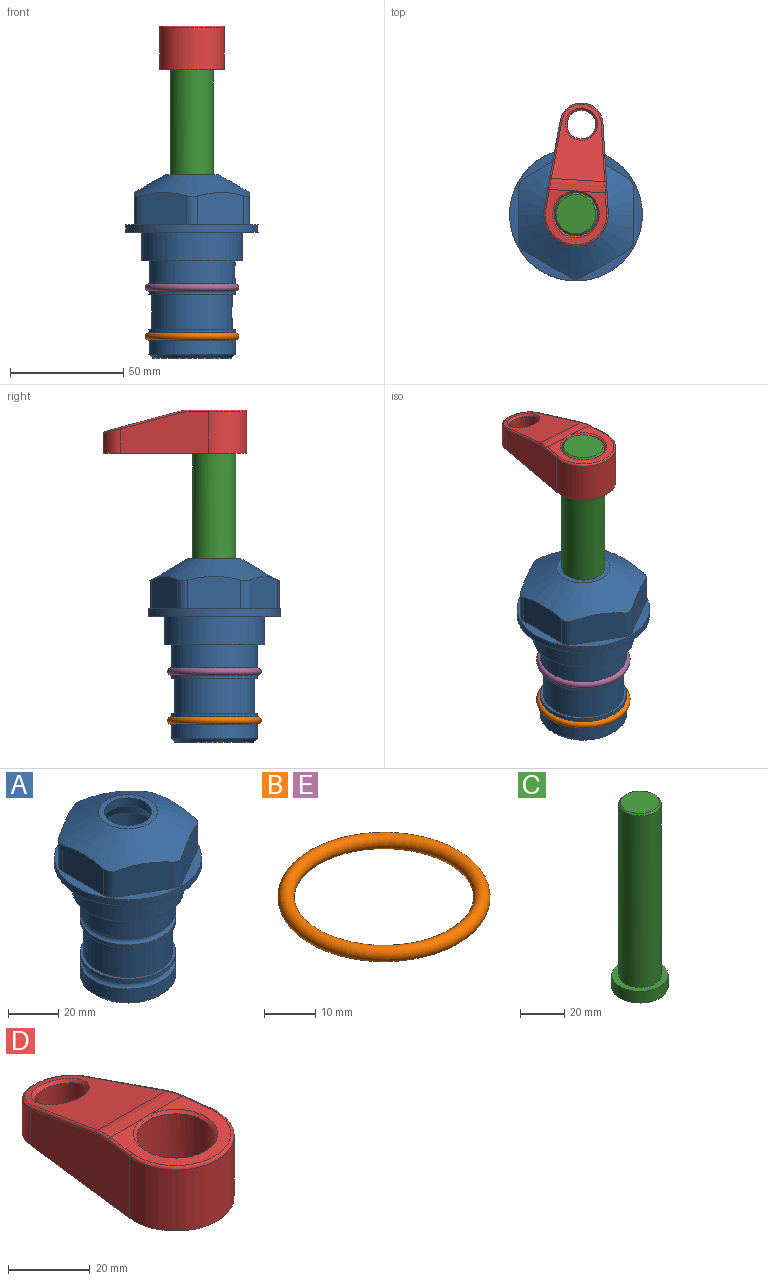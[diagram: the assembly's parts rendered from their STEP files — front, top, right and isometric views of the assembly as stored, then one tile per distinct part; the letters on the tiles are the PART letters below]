
ASSEMBLY  parts=5 mates=4
PART A: 36 faces, bbox 58.7x58.7x81 mm
  f0: cylinder r=17.78mm len=35.56mm, axis (0,0,1), area 1670.8mm2, adj f23,f24,f31
  f1: cylinder r=19.05mm len=38.1mm, axis (0,0,1), area 1191.9mm2, adj f26,f27,f30
  f2: plane 58.66x58.66mm, normal (0,0,-1), area 1150.6mm2, adj f3,f28
  f3: cylinder r=29.33mm len=58.66mm, axis (0,0,-1), area 585.1mm2, adj f2,f4
  f4: plane 58.66x58.66mm, normal (0,0,1), area 475.9mm2, adj f3,f5,f6,f7,f8,f9,f10,f11
  f5: plane 20.32x14.34mm, normal (-0.5,0.87,0), area 324.4mm2, adj f4,f15,f16,f17
  f6: plane 20.32x14.34mm, normal (0.5,0.87,0), area 324.4mm2, adj f4,f14,f15,f17
  f7: plane 23.48x14.34mm, normal (1,0,0), area 324.4mm2, adj f4,f13,f14,f17
  f8: plane 20.32x14.34mm, normal (0.5,-0.87,0), area 324.4mm2, adj f4,f12,f13,f17
  f9: plane 20.32x14.34mm, normal (-0.5,-0.87,0), area 324.4mm2, adj f4,f11,f12,f17
  f10: plane 23.48x14.34mm, normal (-1,0,0), area 324.4mm2, adj f4,f11,f16,f17
  f11: cylinder r=5.08mm len=12.85mm, axis (0,0,-1), area 67.2mm2, adj f4,f9,f10,f17
  f12: cylinder r=5.08mm len=12.85mm, axis (0,0,-1), area 67.2mm2, adj f4,f8,f9,f17
  f13: cylinder r=5.08mm len=12.85mm, axis (0,0,-1), area 67.2mm2, adj f4,f7,f8,f17
  f14: cylinder r=5.08mm len=12.85mm, axis (0,0,-1), area 67.2mm2, adj f4,f6,f7,f17
  f15: cylinder r=5.08mm len=12.85mm, axis (0,0,-1), area 67.2mm2, adj f4,f5,f6,f17
  f16: cylinder r=5.08mm len=12.85mm, axis (0,0,-1), area 67.2mm2, adj f4,f5,f10,f17
  f17: cone r=11.73mm half-angle=60deg, axis (0,0,-1), area 2071.8mm2, adj f5,f6,f7,f8,f9,f10,f11,f12
  f18: plane 23.46x23.46mm, normal (0,0,1), area 147.4mm2, adj f17,f35
  f19: plane 34.93x34.93mm, normal (0,0,-1), area 958mm2, adj f29
  f20: cylinder r=19.05mm len=38.1mm, axis (0,0,1), area 760.1mm2, adj f21,f29
  f21: torus R=19.05mm, axis (0,0,1), area 565.3mm2, adj f20,f22
  f22: cylinder r=19.05mm len=38.1mm, axis (0,0,1), area 190mm2, adj f21,f23
  f23: plane 38.1x38.1mm, normal (0,0,1), area 146.9mm2, adj f0,f22
  f24: plane 38.1x38.1mm, normal (0,0,-1), area 146.9mm2, adj f0,f25
  f25: cylinder r=19.05mm len=38.1mm, axis (0,0,1), area 190mm2, adj f24,f26
  f26: torus R=19.05mm, axis (0,0,1), area 565.3mm2, adj f1,f25
  f27: plane 44.45x44.45mm, normal (0,0,-1), area 411.7mm2, adj f1,f28
  f28: cylinder r=22.23mm len=44.45mm, axis (0,0,1), area 1773.5mm2, adj f2,f27
  f29: cone r=19.05mm half-angle=45deg, axis (0,0,1), area 257.5mm2, adj f19,f20
  f30: cylinder r=3.17mm len=6.75mm, axis (-1,0,0), area 128mm2, adj f1,f33
  f31: cylinder r=3.17mm len=6.35mm, axis (-1,0,0), area 102.5mm2, adj f0,f33
  f32: plane 25.4x25.4mm, normal (0,0,1), area 506.7mm2, adj f33
  f33: cylinder r=12.7mm len=66.42mm, axis (0,0,-1), area 5236.2mm2, adj f30,f31,f32,f34
  f34: cone r=9.53mm half-angle=30deg, axis (0,0,-1), area 443.4mm2, adj f33,f35
  f35: cylinder r=9.53mm len=19.05mm, axis (0,0,-1), area 240.9mm2, adj f18,f34
PART B: 1 faces, bbox 44.7x44.7x3.2 mm
  f0: torus R=19.05mm, axis (0,0,1), area 1193.9mm2
PART C: 6 faces, bbox 25.4x25.4x101.6 mm
  f0: plane 17.46x17.46mm, normal (0,0,1), area 239.5mm2, adj f5
  f1: plane 25.4x25.4mm, normal (0,0,-1), area 506.7mm2, adj f2
  f2: cylinder r=12.7mm len=25.4mm, axis (0,0,1), area 506.7mm2, adj f1,f3
  f3: plane 25.4x25.4mm, normal (0,0,1), area 221.7mm2, adj f2,f4
  f4: cylinder r=9.53mm len=94.46mm, axis (0,0,1), area 5653mm2, adj f3,f5
  f5: cone r=8.73mm half-angle=45deg, axis (0,0,-1), area 64.4mm2, adj f0,f4
PART D: 31 faces, bbox 31.7x65.5x19.8 mm
  f0: plane 39.12x18.26mm, normal (0.99,0.12,0), area 612.2mm2, adj f1,f4,f7,f11,f13,f15
  f1: cylinder r=9.53mm len=18.91mm, axis (0,0,-1), area 296.1mm2, adj f0,f2,f7,f17
  f2: plane 39.12x18.26mm, normal (-0.99,0.12,0), area 612.2mm2, adj f1,f4,f7,f12,f14,f16
  f3: cylinder r=6.35mm len=12.7mm, axis (0,0,-1), area 362.4mm2, adj f7,f18
  f4: cylinder r=14.29mm len=28.58mm, axis (0,0,-1), area 882.2mm2, adj f0,f2,f7,f10
  f5: cylinder r=9.53mm len=19.05mm, axis (0,0,-1), area 1092.6mm2, adj f7,f19,f20
  f6: plane 26.99x23.69mm, normal (0,0,1), area 216.2mm2, adj f9,f10,f11,f12,f19
  f7: plane 63.5x28.58mm, normal (0,0,-1), area 661.8mm2, adj f0,f1,f2,f3,f4,f5,f22,f23
  f8: plane 33.52x23.6mm, normal (0,0.26,0.97), area 486mm2, adj f9,f15,f16,f17,f18
  f9: cylinder r=19.05mm len=24.72mm, axis (1,0,0), area 120.4mm2, adj f6,f8,f13,f14,f20
  f10: torus R=13.49mm, axis (0,0,1), area 59mm2, adj f4,f6,f11,f12
  f11: cylinder r=0.79mm len=8.67mm, axis (0.12,-0.99,0), area 10.8mm2, adj f0,f6,f10,f13
  f12: cylinder r=0.79mm len=8.67mm, axis (0.12,0.99,0), area 10.8mm2, adj f2,f6,f10,f14
  f13: bspline ~4.95x1.42mm, area 6.1mm2, adj f0,f9,f11,f15
  f14: bspline ~4.95x1.42mm, area 6.1mm2, adj f2,f9,f12,f16
  f15: cylinder r=0.79mm len=25.95mm, axis (0.12,-0.96,0.26), area 32.9mm2, adj f0,f8,f13,f17
  f16: cylinder r=0.79mm len=25.95mm, axis (0.12,0.96,-0.26), area 32.9mm2, adj f2,f8,f14,f17
  f17: bspline ~18.91x8.38mm, area 30mm2, adj f1,f8,f15,f16
  f18: bspline ~14.29x14.29mm, area 48.3mm2, adj f3,f8
  f19: cone r=9.53mm half-angle=45deg, axis (0,0,1), area 66.5mm2, adj f5,f6,f20
  f20: bspline ~3.22x0.96mm, area 3.5mm2, adj f5,f9,f19
  f21: plane 2.75x2.72mm, normal (0,0,-1), area 2.9mm2, adj f23,f25,f28
  f22: plane 23.05x15.88mm, normal (-0.99,-0.12,0), area 323.6mm2, adj f7,f25,f26,f27,f28,f29
  f23: plane 23.05x15.88mm, normal (0.99,-0.12,0), area 323.6mm2, adj f7,f21,f25,f27,f28,f30
  f24: cylinder r=9.53mm len=10.69mm, axis (0,0,-1), area 114.7mm2, adj f7,f27,f29,f30
  f25: cylinder r=12.7mm len=20.59mm, axis (0,0,-1), area 381.1mm2, adj f7,f21,f22,f23,f26,f28
  f26: plane 2.75x2.72mm, normal (0,0,-1), area 2.9mm2, adj f22,f25,f28
  f27: plane 19.72x18.37mm, normal (0,-0.26,-0.97), area 291.8mm2, adj f22,f23,f24,f28,f29,f30
  f28: cylinder r=15.88mm len=19.92mm, axis (1,0,0), area 54.8mm2, adj f21,f22,f23,f25,f26,f27
  f29: cylinder r=1.59mm len=11mm, axis (0,0,-1), area 34.7mm2, adj f7,f22,f24,f27
  f30: cylinder r=1.59mm len=11mm, axis (0,0,-1), area 34.7mm2, adj f7,f23,f24,f27
PART E: same geometry as B
PLACE A at identity fixed
PLACE B t=(0,0,-21.59)mm
PLACE C rot(axis=(0,0,-1),3.5deg) t=(0,0,27.55)mm
PLACE D rot(axis=(0,0,-1),3.5deg) t=(0,0,27.55)mm
PLACE E at identity
MATE cylindrical C.f2 <-> A.f0  axis (0,0,-1) through (0,0,-10.55)mm
MATE fastened D.f4 <-> C.f2  axis (0,0,1) through (0,0,91.05)mm
MATE fastened E.f0 <-> A.f0  axis (0,0,1) through (0,0,-24.51)mm
MATE fastened B.f0 <-> A.f0  axis (0,0,1) through (0,0,-46.1)mm
